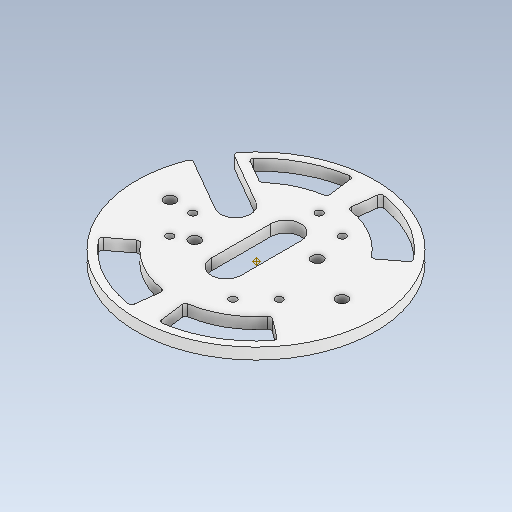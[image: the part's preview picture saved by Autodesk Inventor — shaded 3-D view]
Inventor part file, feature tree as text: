
AUTODESK INVENTOR PART (.ipt)
format: ipt  version: 2021 (Build 250183000, 183)  size: 187,904 bytes
history: mixed  units: in
note: dims shown in document units (in); Inventor stores cm internally (conversion verified against a paired STEP export)
features: move_body x1, fillet x1, imported_body x1
ambient origin geometry x8: Origin, YZ Plane, XZ Plane, XY Plane, X Axis, Y Axis, Z Axis, Center Point
bodies: Solid1 (imported_parasolid)
feature tree (3):
  move_body  "Move Body1"
  fillet  "Fillet3"  Radius=0.0415in
  imported_body  NMx_Import_Brep_tag  [imported B-rep: ~54 faces, bbox_mm=[169.039301, 9.525, 188.282505]]
